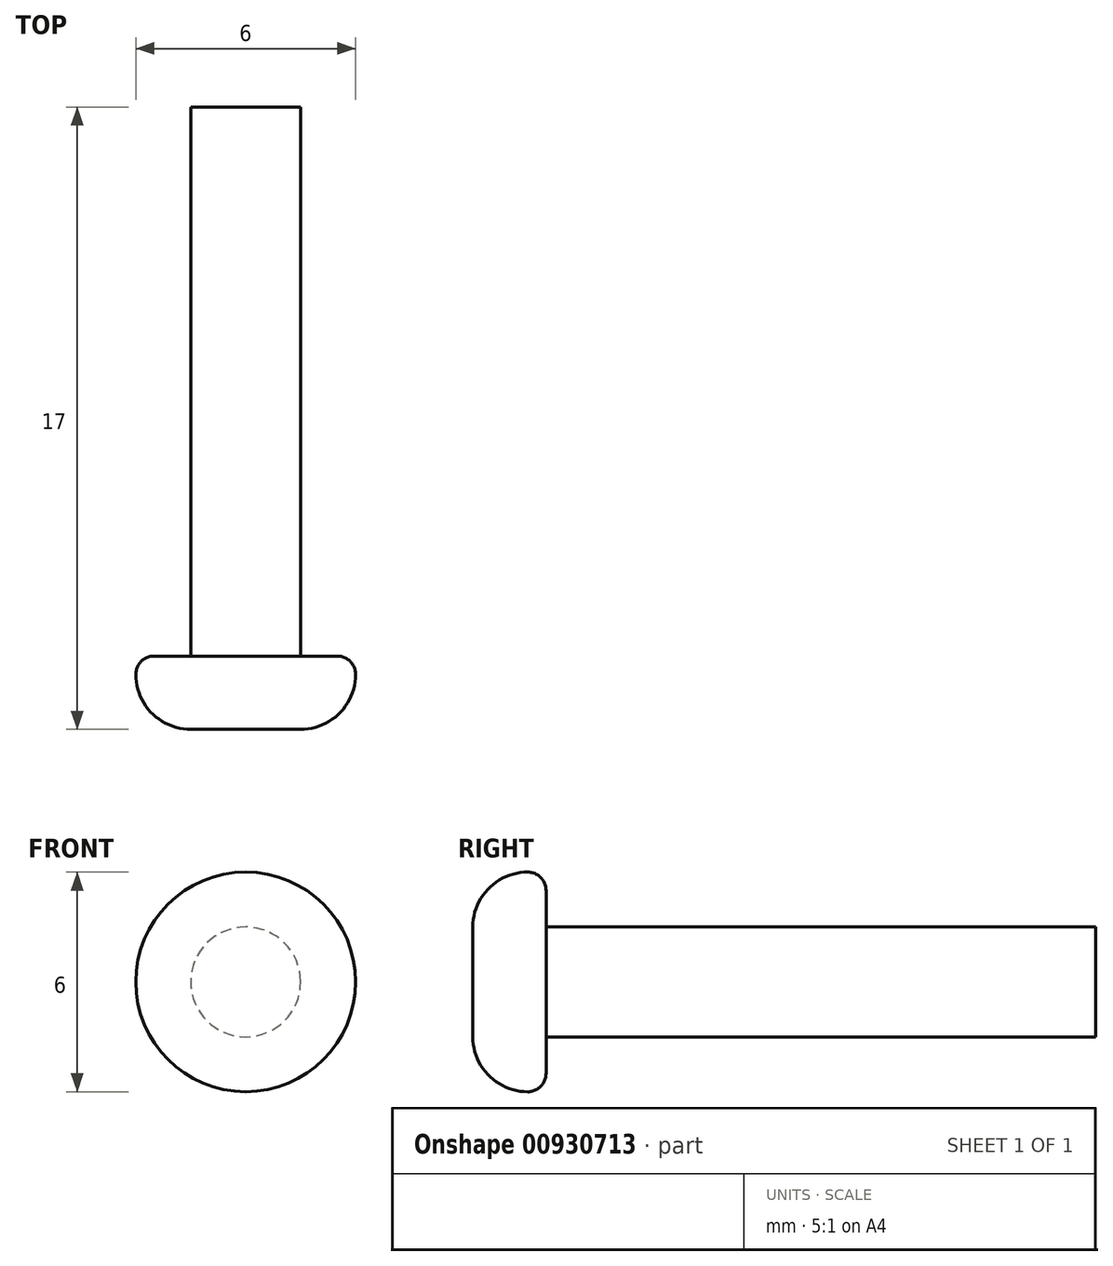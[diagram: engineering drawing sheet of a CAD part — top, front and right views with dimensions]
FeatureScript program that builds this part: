
annotation { "Feature Type Name" : "Feature", "Feature Type Description" : "" }
export const myFeature = defineFeature(function(context is Context, id is Id, definition is map)
    precondition{}
    {
        {
            var Q0;
            Q0=qCreatedBy(makeId("Front.planeOp"),FACE);
            var sketch = newSketch(context, id + "F0", { "sketchPlane" : qUnion([Q0])});
            skCircle(sketch, "E0", {"center": v(0, 0) * mm, "radius": 1.5 * mm});
            skSolve(sketch);
        }
        {
            var Q0;
            Q0=makeQuery(id+"F0.imprint","IMPRINT",FACE,{"disambiguationData":[TD([[makeQuery(id+"F0.imprint","IMPRINT",EDGE,{"derivedFrom":sQuery(id+"F0.wireOp",EDGE,"E0")}),1.0]])]});
            var Q1;
            Q1=sQuery(id+"F0.wireOp",EDGE,"E0");
            extrude(context, id + "F1", {"entities" : qUnion([Q0]), "surfaceEntities" : qUnion([Q1]), "oppositeDirection" : true, "depth" : 15 * mm, "offsetDistance" : 25 * mm});
        }
        {
            var Q0;
            Q0=makeQuery(id+"F1.opExtrude","CAP_FACE",FACE,{"disambiguationData":[OSD([sQuery(id+"F0.wireOp",EDGE,"E0")])],"isStart":true});
            var sketch = newSketch(context, id + "F2", { "sketchPlane" : qUnion([Q0])});
            skCircle(sketch, "E1", {"center": v(0, 0) * mm, "radius": 3 * mm});
            skSolve(sketch);
        }
        {
            var Q0;
            Q0=qSketchRegion(id+"F2",true);
            extrude(context, id + "F3", {"entities" : qUnion([Q0]), "operationType" : NewBodyOperationType.ADD, "depth" : 2 * mm, "offsetDistance" : 25 * mm});
        }
        {
            var Q0;
            Q0=makeQuery(id+"F3.opExtrude","CAP_EDGE",EDGE,{"disambiguationData":[OSD([sQuery(id+"F2.wireOp",EDGE,"E1")])],"isStart":false});
            fillet(context, id + "F4", {"entities" : qUnion([Q0]), "radius" : 1.5 * mm, "tangentPropagation" : true, "allowEdgeOverflow" : false});
        }
        {
            var Q0;
            Q0=makeQuery(id+"F3.opExtrude","CAP_EDGE",EDGE,{"disambiguationData":[OSD([sQuery(id+"F2.wireOp",EDGE,"E1")])],"isStart":true});
            fillet(context, id + "F5", {"entities" : qUnion([Q0]), "radius" : 0.5 * mm, "tangentPropagation" : true, "allowEdgeOverflow" : false});
        }
    });
